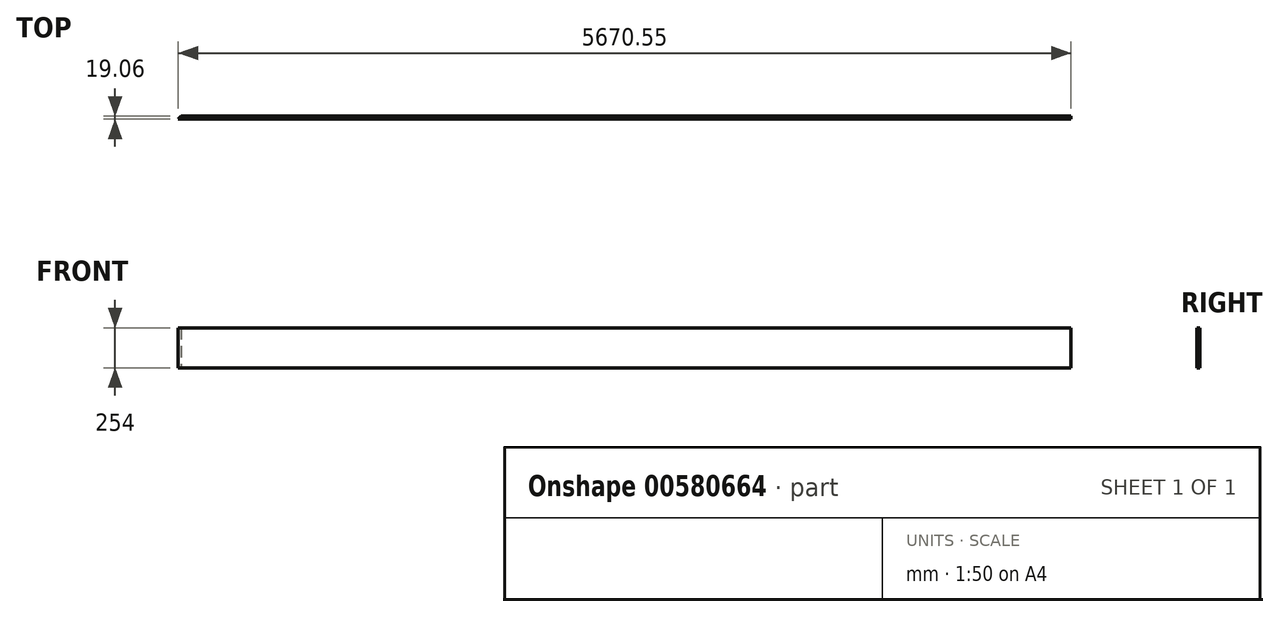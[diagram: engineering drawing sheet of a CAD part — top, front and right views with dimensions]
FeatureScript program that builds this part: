
annotation { "Feature Type Name" : "Feature", "Feature Type Description" : "" }
export const myFeature = defineFeature(function(context is Context, id is Id, definition is map)
    precondition{}
    {
        {
            var Q0;
            Q0=qCreatedBy(makeId("Top.planeOp"),FACE);
            var sketch = newSketch(context, id + "F0", { "sketchPlane" : qUnion([Q0])});
            skLineSegment(sketch, "E0.bottom", {"start": v(1978.03, -9.53) * mm, "end": v(-3692.52, -9.53) * mm});
            skLineSegment(sketch, "E0.top", {"start": v(1978.03, 9.52) * mm, "end": v(-3673.47, 9.52) * mm});
            skPoint(sketch, "E0.middle", {"position": v(0, 0) * mm});
            skLineSegment(sketch, "E1", {"start": v(-3692.52, -9.53) * mm, "end": v(-3673.47, 9.52) * mm});
            skPoint(sketch, "E2.orphan", {"position": v(-3660.78, 9.52) * mm});
            skPoint(sketch, "E0.left.end.orphan", {"position": v(3692.52, 9.53) * mm});
            skLineSegment(sketch, "E3", {"start": v(1978.03, 9.53) * mm, "end": v(1978.03, -9.53) * mm});
            skSolve(sketch);
        }
        {
            var Q0;
            Q0=makeQuery(id+"F0.imprint","IMPRINT",FACE,{"disambiguationData":[TD([[makeQuery(id+"F0.imprint","IMPRINT",EDGE,{"derivedFrom":sQuery(id+"F0.wireOp",EDGE,"E0.bottom")}),-1.0]])]});
            extrude(context, id + "F1", {"entities" : qUnion([Q0]), "depth" : 254 * mm, "offsetDistance" : 25.4 * mm});
        }
    });
